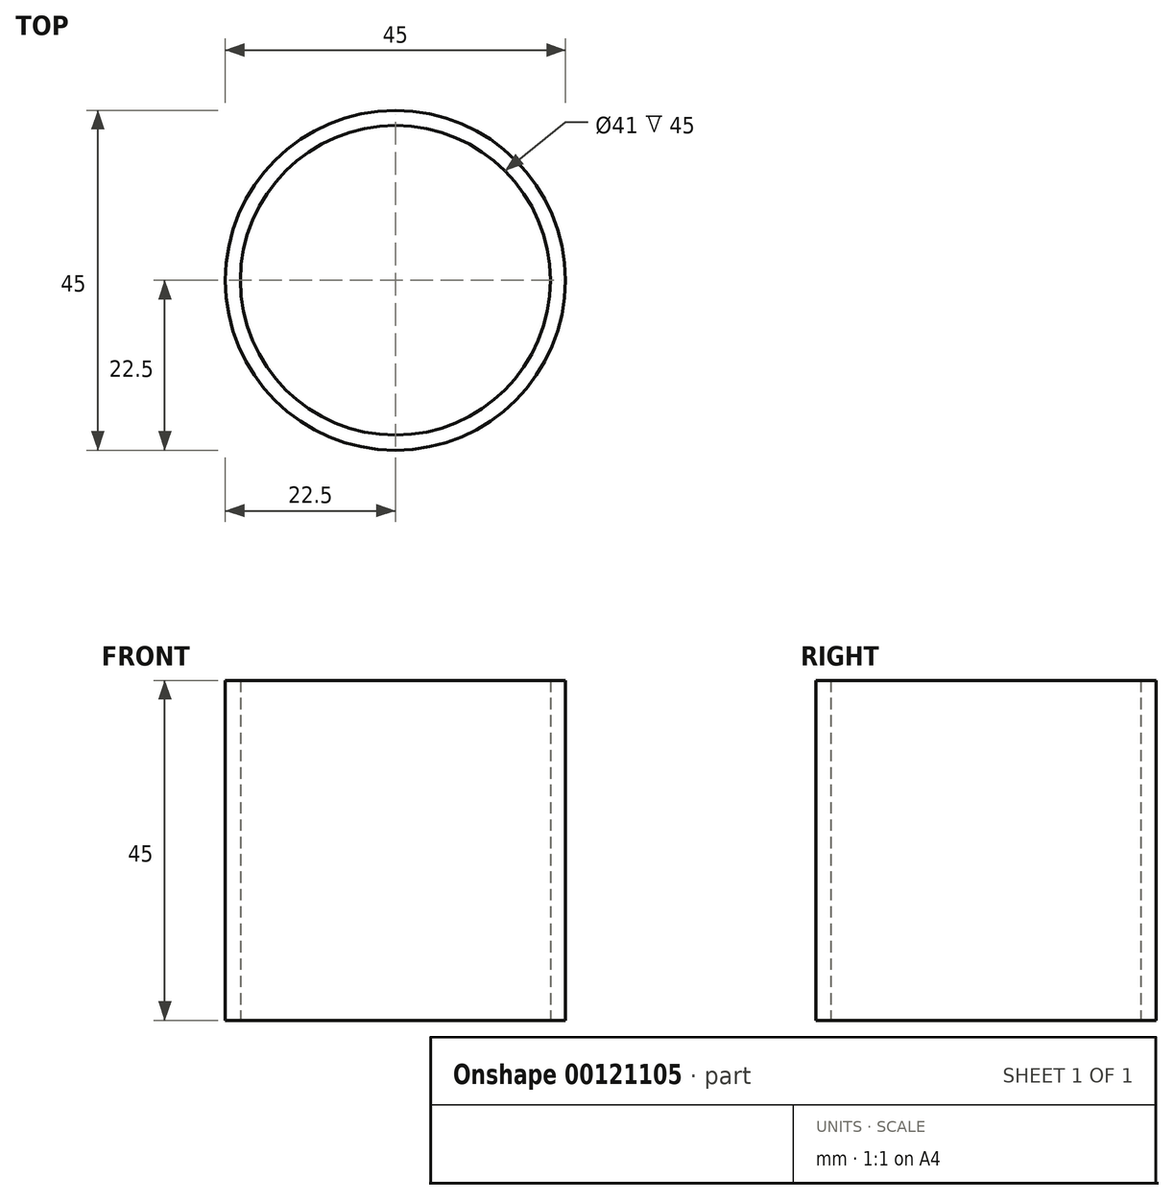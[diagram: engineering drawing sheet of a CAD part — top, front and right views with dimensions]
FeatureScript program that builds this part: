
annotation { "Feature Type Name" : "Feature", "Feature Type Description" : "" }
export const myFeature = defineFeature(function(context is Context, id is Id, definition is map)
    precondition{}
    {
        {
            var Q0;
            Q0=qCreatedBy(makeId("Top.planeOp"),FACE);
            var sketch = newSketch(context, id + "F0", { "sketchPlane" : qUnion([Q0])});
            skCircle(sketch, "E0", {"center": v(0, 0) * mm, "radius": 22.5 * mm});
            skCircle(sketch, "E1", {"center": v(0, 0) * mm, "radius": 20.5 * mm});
            skSolve(sketch);
        }
        {
            var Q0;
            Q0=qSketchRegion(id+"F0",true);
            extrude(context, id + "F1", {"entities" : qUnion([Q0]), "depth" : 10 * mm});
        }
        {
            var Q0;
            Q0=qCreatedBy(makeId("Top.planeOp"),FACE);
            cPlane(context, id + "F2", {"entities" : qUnion([Q0]), "cplaneType" : CPlaneType.OFFSET, "offset" : 10 * mm, "width" : 150 * mm, "height" : 150 * mm});
        }
        {
            var Q0;
            Q0=qCreatedBy(id+"F2.planeOp",FACE);
            var sketch = newSketch(context, id + "F3", { "sketchPlane" : qUnion([Q0])});
            skCircle(sketch, "E2", {"center": v(0, 0) * mm, "radius": 22.5 * mm});
            skCircle(sketch, "E3", {"center": v(0, 0) * mm, "radius": 20.5 * mm});
            skSolve(sketch);
        }
        {
            var Q0;
            Q0=qSketchRegion(id+"F3",true);
            extrude(context, id + "F4", {"entities" : qUnion([Q0]), "operationType" : NewBodyOperationType.ADD, "depth" : 35 * mm});
        }
    });
